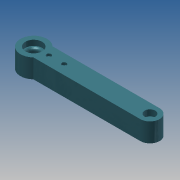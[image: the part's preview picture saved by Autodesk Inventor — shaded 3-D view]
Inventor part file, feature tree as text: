
AUTODESK INVENTOR PART (.ipt)
format: ipt  version: 2013 (Build 170138000, 138)  size: 134,144 bytes
history: native  units: mm
features: extrude x6, sketch x6, fillet x1
ambient origin geometry x8: Origin, YZ Plane, XZ Plane, XY Plane, X Axis, Y Axis, Z Axis, Center Point
bodies: Solid1 (feature_tree)
feature tree (13):
  extrude  "Extrusion1"  Depth=12.6mm
  extrude  "Extrusion2"  Depth=8.5mm
  extrude  "Extrusion3"  Depth=22.0mm
  extrude  "Extrusion4"  Depth=20.0mm
  extrude  "Extrusion5"  Depth=7.0mm TaperAngle=0.0deg
  extrude  "Extrusion6"  Depth=3.5mm
  fillet  "Fillet1"  Radius=35.0mm
  sketch  "Sketch1"  dims[d0=153.0mm d2=12.6mm]
  sketch  "Sketch2"  dims[d3=15.0mm d4=8.5mm]
  sketch  "Sketch4"  dims[d5=25.0mm d6=0.0mm d7=22.0mm]
  sketch  "Sketch5"  dims[d9=7.0mm d10=0.0mm d16=20.0mm]
  sketch  "Sketch6"  dims[d17=40.0mm d18=7.0mm d19=0.0mm]
  sketch  "Sketch7"  dims[d21=3.0mm d22=0.0mm d23=3.5mm d24=35.0mm d26=10.0mm d27=0.0mm d28=6.0mm d30=14.0mm d32=8.0mm d33=0.0mm d34=3.5mm]
